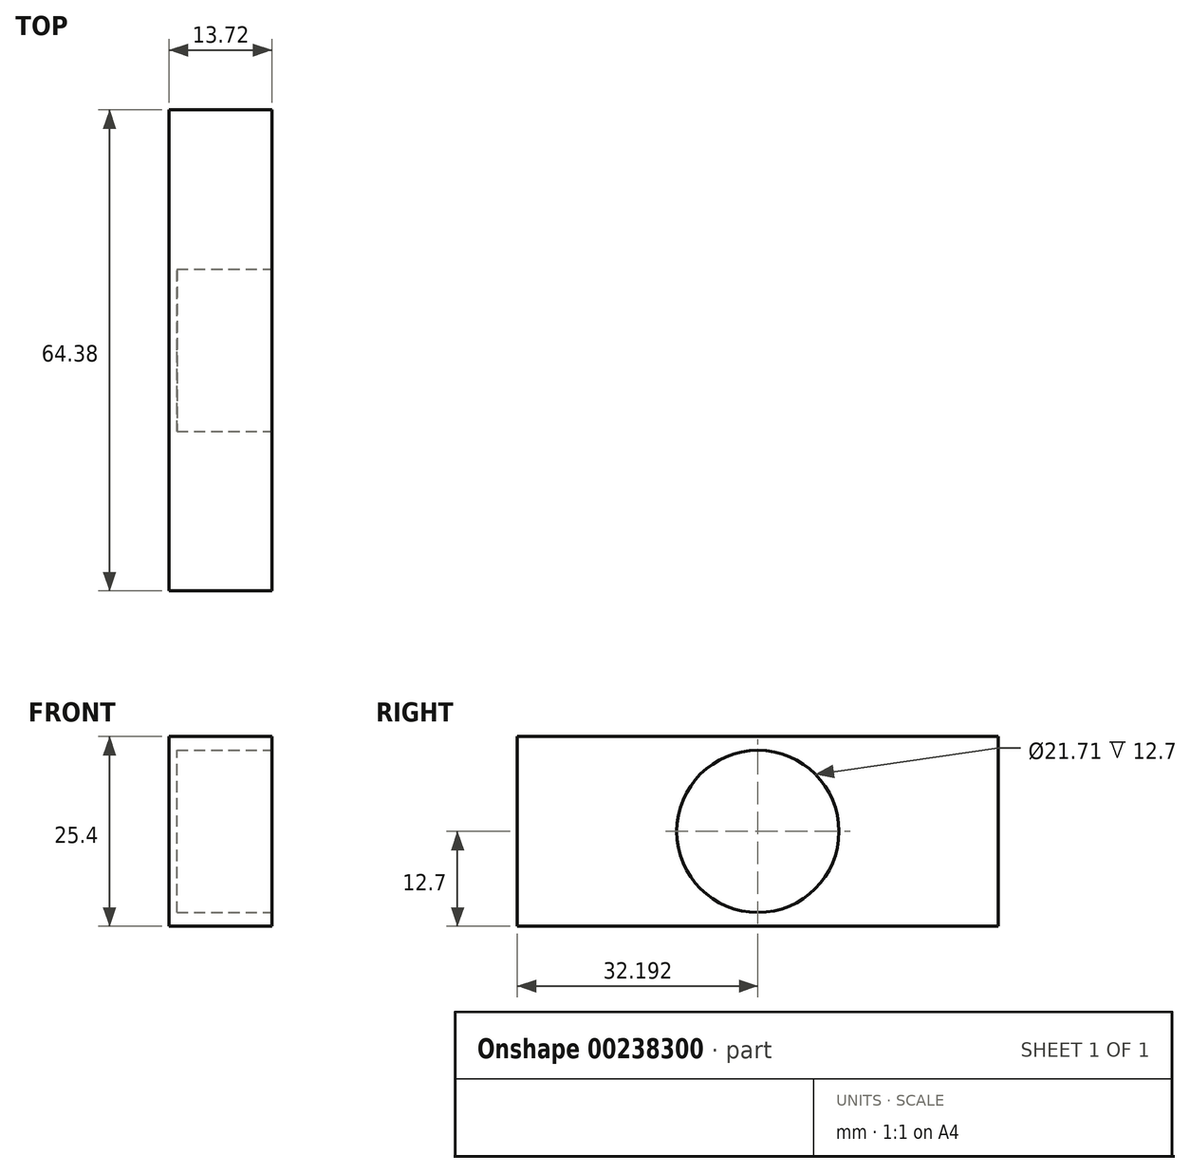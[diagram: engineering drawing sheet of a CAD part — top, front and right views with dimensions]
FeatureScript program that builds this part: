
annotation { "Feature Type Name" : "Feature", "Feature Type Description" : "" }
export const myFeature = defineFeature(function(context is Context, id is Id, definition is map)
    precondition{}
    {
        {
            var Q0;
            Q0=qCreatedBy(makeId("Top.planeOp"),FACE);
            var sketch = newSketch(context, id + "F0", { "sketchPlane" : qUnion([Q0])});
            skLineSegment(sketch, "E0.bottom", {"start": v(0, 0) * mm, "end": v(13.72, 0) * mm});
            skLineSegment(sketch, "E0.top", {"start": v(0, -64.38) * mm, "end": v(13.72, -64.38) * mm});
            skLineSegment(sketch, "E0.left", {"start": v(0, 0) * mm, "end": v(0, -64.38) * mm});
            skLineSegment(sketch, "E0.right", {"start": v(13.72, 0) * mm, "end": v(13.72, -64.38) * mm});
            skSolve(sketch);
        }
        {
            var Q0;
            Q0=makeQuery(id+"F0.imprint","IMPRINT",FACE,{"disambiguationData":[TD([[makeQuery(id+"F0.imprint","IMPRINT",EDGE,{"derivedFrom":sQuery(id+"F0.wireOp",EDGE,"E0.bottom")}),-1.0]])]});
            extrude(context, id + "F1", {"entities" : qUnion([Q0]), "depth" : 25.4 * mm});
        }
        {
            var Q0;
            Q0=makeQuery(id+"F1.opExtrude","SWEPT_FACE",FACE,{"disambiguationData":[OSD([sQuery(id+"F0.wireOp",EDGE,"E0.right")])]});
            var sketch = newSketch(context, id + "F2", { "sketchPlane" : qUnion([Q0])});
            skCircle(sketch, "E1", {"center": v(-32.19, 12.7) * mm, "radius": 10.85 * mm});
            skPoint(sketch, "E1.centerSnap0", {"position": v(-32.19, 0) * mm});
            skPoint(sketch, "E1.centerSnap1", {"position": v(0, 12.7) * mm});
            skSolve(sketch);
        }
        {
            var Q0;
            Q0=makeQuery(id+"F2.imprint","IMPRINT",FACE,{"disambiguationData":[TD([[makeQuery(id+"F2.imprint","IMPRINT",EDGE,{"derivedFrom":sQuery(id+"F2.wireOp",EDGE,"E1")}),1.0]])]});
            var Q1;
            Q1=sQuery(id+"F2.wireOp",EDGE,"E1");
            extrude(context, id + "F3", {"entities" : qUnion([Q0]), "operationType" : NewBodyOperationType.REMOVE, "surfaceEntities" : qUnion([Q1]), "oppositeDirection" : true, "depth" : 12.7 * mm});
        }
    });
